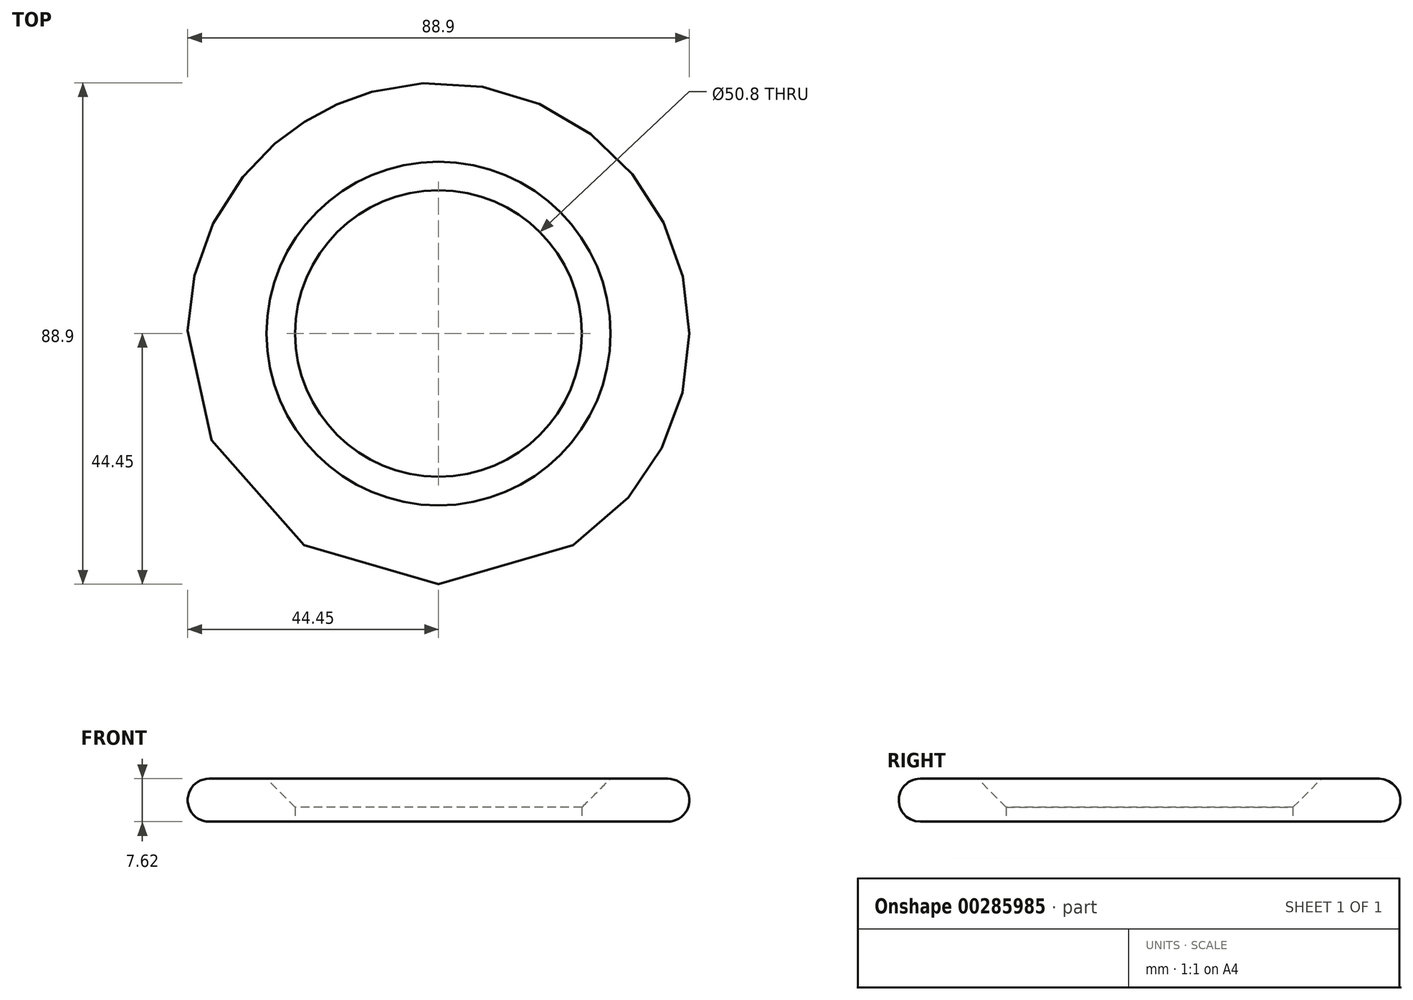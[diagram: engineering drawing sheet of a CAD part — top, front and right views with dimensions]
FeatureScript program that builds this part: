
annotation { "Feature Type Name" : "Feature", "Feature Type Description" : "" }
export const myFeature = defineFeature(function(context is Context, id is Id, definition is map)
    precondition{}
    {
        {
            var Q0;
            Q0=qCreatedBy(makeId("Top.planeOp"),FACE);
            var sketch = newSketch(context, id + "F0", { "sketchPlane" : qUnion([Q0])});
            skCircle(sketch, "E0", {"center": v(0, 0) * mm, "radius": 44.45 * mm});
            skCircle(sketch, "E1", {"center": v(0, 0) * mm, "radius": 25.4 * mm});
            skSolve(sketch);
        }
        {
            var Q0;
            Q0=makeQuery(id+"F0.imprint","IMPRINT",FACE,{"disambiguationData":[TD([[makeQuery(id+"F0.imprint","IMPRINT",EDGE,{"derivedFrom":sQuery(id+"F0.wireOp",EDGE,"E0")}),1.0]])]});
            extrude(context, id + "F1", {"entities" : qUnion([Q0]), "depth" : 7.62 * mm});
        }
        {
            var Q0;
            Q0=makeQuery(id+"F1.opExtrude","CAP_EDGE",EDGE,{"disambiguationData":[OSD([sQuery(id+"F0.wireOp",EDGE,"E1")])],"isStart":false});
            chamfer(context, id + "F2", {"entities" : qUnion([Q0]), "width" : 5.08 * mm, "tangentPropagation" : true});
        }
        {
            var Q0;
            Q0=makeQuery(id+"F1.opExtrude","SWEPT_FACE",FACE,{"disambiguationData":[OSD([sQuery(id+"F0.wireOp",EDGE,"E0")])]});
            fillet(context, id + "F3", {"entities" : qUnion([Q0]), "radius" : 3.8 * mm, "tangentPropagation" : true, "allowEdgeOverflow" : false});
        }
    });
